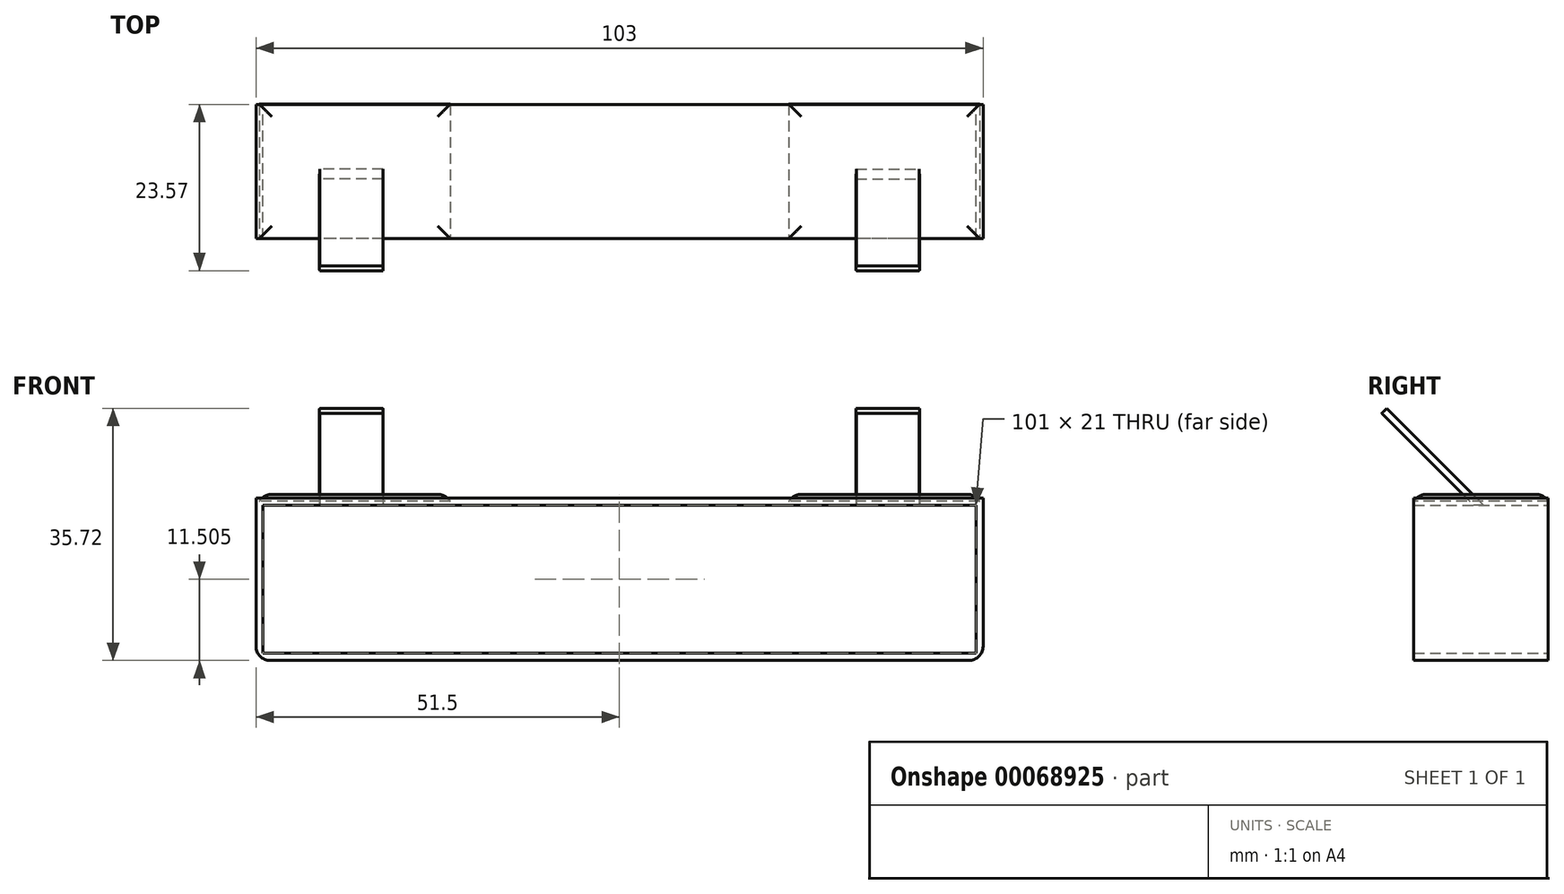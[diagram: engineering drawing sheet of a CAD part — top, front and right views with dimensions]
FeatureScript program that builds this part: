
annotation { "Feature Type Name" : "Feature", "Feature Type Description" : "" }
export const myFeature = defineFeature(function(context is Context, id is Id, definition is map)
    precondition{}
    {
        {
            var Q0;
            Q0=qCreatedBy(makeId("Front.planeOp"),FACE);
            var sketch = newSketch(context, id + "F0", { "sketchPlane" : qUnion([Q0])});
            skCircle(sketch, "E0", {"center": v(-38, 21.56) * mm, "radius": 7 * mm});
            skLineSegment(sketch, "E1", {"start": v(-38, 21.56) * mm, "end": v(-21.61, 21.56) * mm, "construction": true});
            skCircle(sketch, "E2", {"center": v(-38, 21.56) * mm, "radius": 4.5 * mm});
            skLineSegment(sketch, "E3.bottom", {"start": v(-50, 22.06) * mm, "end": v(0, 22.06) * mm});
            skLineSegment(sketch, "E3.top", {"start": v(-50, 21.06) * mm, "end": v(0, 21.06) * mm});
            skLineSegment(sketch, "E3.left", {"start": v(-50, 22.06) * mm, "end": v(-50, 21.06) * mm});
            skLineSegment(sketch, "E3.right", {"start": v(0, 22.06) * mm, "end": v(0, 21.06) * mm});
            skLineSegment(sketch, "E4", {"start": v(-50, 21.56) * mm, "end": v(0, 21.56) * mm, "construction": true});
            skLineSegment(sketch, "E5", {"start": v(0, 53.95) * mm, "end": v(0, 2.95) * mm, "construction": true});
            skLineSegment(sketch, "E6.MirrorCS", {"start": v(-50, 21.06) * mm, "end": v(-50, 22.06) * mm});
            skLineSegment(sketch, "E7.MirrorCS", {"start": v(0, 21.06) * mm, "end": v(0, 22.06) * mm});
            skCircle(sketch, "E8.MirrorC", {"center": v(38, 21.56) * mm, "radius": 7 * mm});
            skLineSegment(sketch, "E9.MirrorCS", {"start": v(50, 21.06) * mm, "end": v(50, 22.06) * mm});
            skCircle(sketch, "E10.MirrorC", {"center": v(38, 21.56) * mm, "radius": 4.5 * mm});
            skLineSegment(sketch, "E11.MirrorCS", {"start": v(50, 22.06) * mm, "end": v(50, 21.06) * mm});
            skLineSegment(sketch, "E12.MirrorCS", {"start": v(50, 22.06) * mm, "end": v(0, 22.06) * mm});
            skLineSegment(sketch, "E13.MirrorCS", {"start": v(50, 21.06) * mm, "end": v(0, 21.06) * mm});
            skLineSegment(sketch, "E14.MirrorCS", {"start": v(38, 21.56) * mm, "end": v(21.61, 21.56) * mm, "construction": true});
            skLineSegment(sketch, "E15.MirrorCS", {"start": v(50, 21.56) * mm, "end": v(0, 21.56) * mm, "construction": true});
            skSolve(sketch);
        }
        {
            var Q0;
            Q0=makeQuery(id+"F0.imprint","IMPRINT",FACE,{"disambiguationData":[TD([[makeQuery(id+"F0.imprint","IMPRINT",EDGE,{"derivedFrom":sQuery(id+"F0.wireOp",EDGE,"E2")}),1.0]])]});
            var Q1;
            Q1=makeQuery(id+"F0.imprint","IMPRINT",FACE,{"disambiguationData":[TD([[makeQuery(id+"F0.imprint","IMPRINT",EDGE,{"derivedFrom":sQuery(id+"F0.wireOp",EDGE,"E10.MirrorC")}),1.0]])]});
            var Q2;
            Q2=sQuery(id+"F0.wireOp",EDGE,"E0");
            extrude(context, id + "F1", {"entities" : qUnion([Q0, Q1]), "surfaceEntities" : qUnion([Q2]), "depth" : 25 * mm});
        }
        {
            var Q0;
            Q0=makeQuery(id+"F1.opExtrude","SWEPT_BODY",BODY,{"disambiguationData":[OSD([sQuery(id+"F0.wireOp",EDGE,"E2"),sQuery(id+"F0.wireOp",EDGE,"E0")])]});
            var Q1;
            Q1=makeQuery(id+"F1.opExtrude","SWEPT_BODY",BODY,{"disambiguationData":[OSD([sQuery(id+"F0.wireOp",EDGE,"E10.MirrorC"),sQuery(id+"F0.wireOp",EDGE,"E8.MirrorC")])]});
            var Q2;
            Q2=sQuery(id+"F0.wireOp",EDGE,"E4");
            var Q3;
            Q3=sQuery(id+"F0.wireOp",EDGE,"E15.MirrorCS");
            transform(context, id + "F2", {"entities" : qUnion([Q0, Q1]), "transformType" : TransformType.ROTATION, "transformAxis" : qUnion([Q3]), "angle" : 45 * degree, "makeCopy" : false});
        }
        {
            var Q0;
            Q0=qCreatedBy(makeId("Right.planeOp"),FACE);
            var sketch = newSketch(context, id + "F3", { "sketchPlane" : qUnion([Q0])});
            skLineSegment(sketch, "E16.bottom", {"start": v(5.54, 27.41) * mm, "end": v(-13.46, 27.41) * mm});
            skLineSegment(sketch, "E16.top", {"start": v(5.54, 26.41) * mm, "end": v(-13.46, 26.41) * mm});
            skLineSegment(sketch, "E16.left", {"start": v(5.54, 27.41) * mm, "end": v(5.54, 26.41) * mm});
            skLineSegment(sketch, "E16.right", {"start": v(-13.46, 27.41) * mm, "end": v(-13.46, 26.41) * mm});
            skLineSegment(sketch, "E17.bottom", {"start": v(-13.46, 26.41) * mm, "end": v(5.54, 26.41) * mm});
            skLineSegment(sketch, "E17.top", {"start": v(-13.46, 3.91) * mm, "end": v(5.54, 3.91) * mm});
            skLineSegment(sketch, "E17.left", {"start": v(-13.46, 26.41) * mm, "end": v(-13.46, 3.91) * mm});
            skLineSegment(sketch, "E17.right", {"start": v(5.54, 26.41) * mm, "end": v(5.54, 3.91) * mm});
            skLineSegment(sketch, "E18", {"start": v(-22.95, 35.2) * mm, "end": v(-12.9, 45.46) * mm, "construction": true});
            skLineSegment(sketch, "E19", {"start": v(-12.9, 45.46) * mm, "end": v(4.92, 27.99) * mm, "construction": true});
            skLineSegment(sketch, "E20", {"start": v(4.92, 27.99) * mm, "end": v(-5.14, 17.73) * mm, "construction": true});
            skLineSegment(sketch, "E21", {"start": v(-5.14, 17.73) * mm, "end": v(-22.95, 35.2) * mm, "construction": true});
            skLineSegment(sketch, "E22", {"start": v(-3.96, 26.41) * mm, "end": v(-3.96, 3.91) * mm, "construction": true});
            skLineSegment(sketch, "E23", {"start": v(-13.46, 15.16) * mm, "end": v(5.54, 15.16) * mm, "construction": true});
            skLineSegment(sketch, "E24.rect.bottom", {"start": v(-13.46, 25.41) * mm, "end": v(5.54, 25.41) * mm});
            skLineSegment(sketch, "E24.rect.top", {"start": v(-13.46, 4.91) * mm, "end": v(5.54, 4.91) * mm});
            skLineSegment(sketch, "E24.rect.left", {"start": v(-13.46, 25.41) * mm, "end": v(-13.46, 4.91) * mm});
            skLineSegment(sketch, "E24.rect.right", {"start": v(5.54, 25.41) * mm, "end": v(5.54, 4.91) * mm});
            skPoint(sketch, "E24.rect.middle", {"position": v(-3.96, 15.16) * mm});
            skSolve(sketch);
        }
        {
            var Q0;
            Q0=makeQuery(id+"F3.imprint","IMPRINT",FACE,{"disambiguationData":[TD([[makeQuery(id+"F3.imprint","IMPRINT",EDGE,{"derivedFrom":sQuery(id+"F3.wireOp",EDGE,"E16.bottom")}),1.0]])]});
            extrude(context, id + "F4", {"entities" : qUnion([Q0]), "depth" : 51 * mm, "hasSecondDirection" : true, "secondDirectionOppositeDirection" : true, "secondDirectionDepth" : 51 * mm});
        }
        {
            var Q0;
            Q0=makeQuery(id+"F3.imprint","IMPRINT",FACE,{"disambiguationData":[TD([[makeQuery(id+"F3.imprint","IMPRINT",EDGE,{"derivedFrom":sQuery(id+"F3.wireOp",EDGE,"E16.bottom")}),1.0]])]});
            extrude(context, id + "F5", {"entities" : qUnion([Q0]), "operationType" : NewBodyOperationType.REMOVE, "oppositeDirection" : true, "depth" : 24 * mm, "hasSecondDirection" : true, "secondDirectionOppositeDirection" : false, "secondDirectionDepth" : 24 * mm});
        }
        {
            var Q0;
            Q0=qCreatedBy(makeId("Front.planeOp"),FACE);
            var sketch = newSketch(context, id + "F6", { "sketchPlane" : qUnion([Q0])});
            skLineSegment(sketch, "E25.rect.bottom", {"start": v(51.5, 26.87) * mm, "end": v(-51.5, 26.87) * mm});
            skLineSegment(sketch, "E25.rect.top", {"start": v(51.5, 3.87) * mm, "end": v(-51.5, 3.87) * mm});
            skLineSegment(sketch, "E25.rect.left", {"start": v(51.5, 26.87) * mm, "end": v(51.5, 3.87) * mm});
            skLineSegment(sketch, "E25.rect.right", {"start": v(-51.5, 26.87) * mm, "end": v(-51.5, 3.87) * mm});
            skPoint(sketch, "E25.rect.middle", {"position": v(0, 15.37) * mm});
            skLineSegment(sketch, "E26.rect.bottom", {"start": v(50.5, 25.87) * mm, "end": v(-50.5, 25.87) * mm});
            skLineSegment(sketch, "E26.rect.top", {"start": v(50.5, 4.87) * mm, "end": v(-50.5, 4.87) * mm});
            skLineSegment(sketch, "E26.rect.left", {"start": v(50.5, 25.87) * mm, "end": v(50.5, 4.87) * mm});
            skLineSegment(sketch, "E26.rect.right", {"start": v(-50.5, 25.87) * mm, "end": v(-50.5, 4.87) * mm});
            skSolve(sketch);
        }
        {
            var Q0;
            Q0=makeQuery(id+"F6.imprint","IMPRINT",FACE,{"disambiguationData":[TD([[makeQuery(id+"F6.imprint","IMPRINT",EDGE,{"derivedFrom":sQuery(id+"F6.wireOp",EDGE,"E25.rect.bottom")}),1.0]])]});
            extrude(context, id + "F7", {"entities" : qUnion([Q0]), "depth" : 13.5 * mm, "hasSecondDirection" : true, "secondDirectionOppositeDirection" : true, "secondDirectionDepth" : 5.5 * mm});
        }
        {
            var Q0;
            Q0=makeQuery(id+"F6.imprint","IMPRINT",FACE,{"disambiguationData":[TD([[makeQuery(id+"F6.imprint","IMPRINT",EDGE,{"derivedFrom":sQuery(id+"F6.wireOp",EDGE,"E26.rect.bottom")}),1.0]])]});
            extrude(context, id + "F8", {"entities" : qUnion([Q0]), "operationType" : NewBodyOperationType.REMOVE, "depth" : 25 * mm, "hasSecondDirection" : true, "secondDirectionOppositeDirection" : true, "secondDirectionDepth" : 25 * mm});
        }
        {
            var Q0;
            {var subQ0=sQuery(id+"F3.wireOp",EDGE,"E17.bottom");var subQ1=sQuery(id+"F3.wireOp",EDGE,"E16.right");var subQ2=sQuery(id+"F3.wireOp",EDGE,"E16.left");var subQ3=sQuery(id+"F3.wireOp",EDGE,"E16.bottom");Q0=makeQuery(id+"F5.boolean.opBoolean","SPLIT",FACE,{"disambiguationData":[TD([makeQuery(id+"F4.opExtrude","CAP_FACE",FACE,{"disambiguationData":[OSD([subQ3,subQ2,subQ1,subQ0])],"isStart":true})])],"derivedFrom":makeQuery(id+"F4.opExtrude","SWEPT_FACE",FACE,{"disambiguationData":[OSD([subQ3])]})});}
            var Q1;
            {var subQ0=sQuery(id+"F3.wireOp",EDGE,"E17.bottom");var subQ1=sQuery(id+"F3.wireOp",EDGE,"E16.right");var subQ2=sQuery(id+"F3.wireOp",EDGE,"E16.left");var subQ3=sQuery(id+"F3.wireOp",EDGE,"E16.bottom");Q1=makeQuery(id+"F5.boolean.opBoolean","SPLIT",FACE,{"disambiguationData":[TD([makeQuery(id+"F4.opExtrude","CAP_FACE",FACE,{"disambiguationData":[OSD([subQ3,subQ2,subQ1,subQ0])],"isStart":false})])],"derivedFrom":makeQuery(id+"F4.opExtrude","SWEPT_FACE",FACE,{"disambiguationData":[OSD([subQ3])]})});}
            fillet(context, id + "F9", {"entities" : qUnion([Q0, Q1]), "radius" : 2 * mm, "tangentPropagation" : true, "allowEdgeOverflow" : false});
        }
        {
            var Q0;
            Q0=makeQuery(id+"F7.opExtrude","SWEPT_EDGE",EDGE,{"disambiguationData":[OSD([sQuery(id+"F6.wireOp",EDGE,"E25.rect.top"),sQuery(id+"F6.wireOp",EDGE,"E25.rect.left")])]});
            var Q1;
            Q1=makeQuery(id+"F7.opExtrude","SWEPT_EDGE",EDGE,{"disambiguationData":[OSD([sQuery(id+"F6.wireOp",EDGE,"E25.rect.top"),sQuery(id+"F6.wireOp",EDGE,"E25.rect.right")])]});
            fillet(context, id + "F10", {"entities" : qUnion([Q0, Q1]), "radius" : 2 * mm, "tangentPropagation" : true, "allowEdgeOverflow" : false});
        }
    });
